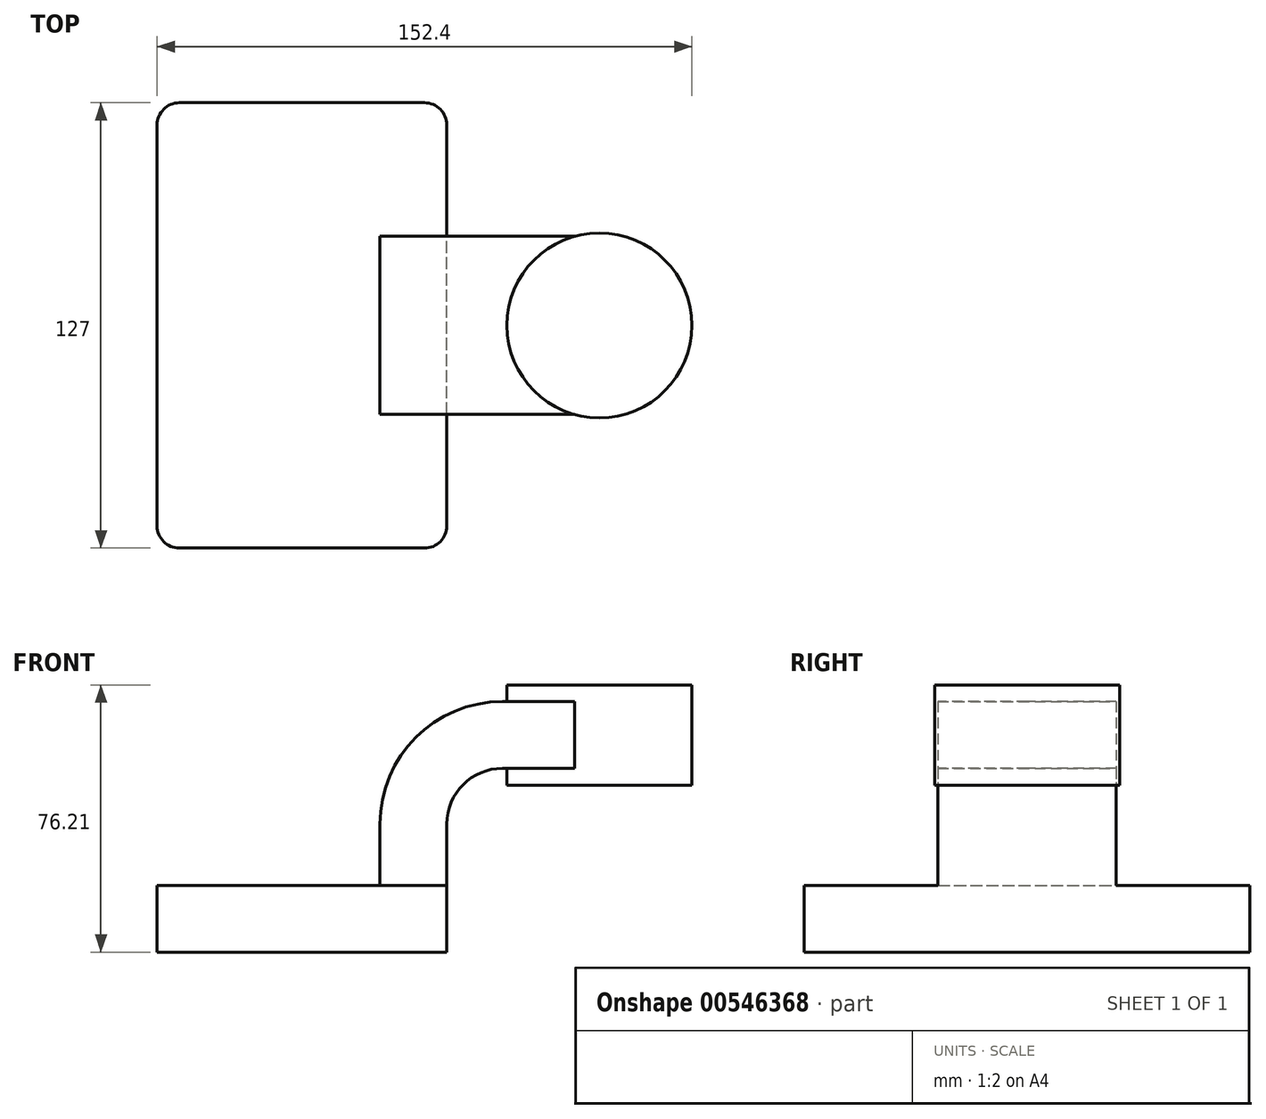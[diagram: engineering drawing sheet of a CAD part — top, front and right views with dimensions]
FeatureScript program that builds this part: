
annotation { "Feature Type Name" : "Feature", "Feature Type Description" : "" }
export const myFeature = defineFeature(function(context is Context, id is Id, definition is map)
    precondition{}
    {
        {
            var Q0;
            Q0=qCreatedBy(makeId("Front.planeOp"),FACE);
            var sketch = newSketch(context, id + "F0", { "sketchPlane" : qUnion([Q0])});
            skLineSegment(sketch, "E0.bottom", {"start": v(-41.28, -9.53) * mm, "end": v(41.28, -9.53) * mm});
            skLineSegment(sketch, "E0.top", {"start": v(-41.28, 9.53) * mm, "end": v(41.27, 9.53) * mm});
            skLineSegment(sketch, "E0.left", {"start": v(-41.27, -9.53) * mm, "end": v(-41.28, 9.53) * mm});
            skLineSegment(sketch, "E0.right", {"start": v(41.28, -9.53) * mm, "end": v(41.27, 9.53) * mm});
            skPoint(sketch, "E0.middle", {"position": v(0, 0) * mm});
            skLineSegment(sketch, "E1.bottom", {"start": v(60.32, 38.1) * mm, "end": v(111.12, 38.1) * mm});
            skLineSegment(sketch, "E1.top", {"start": v(60.32, 66.67) * mm, "end": v(111.12, 66.67) * mm});
            skLineSegment(sketch, "E1.left", {"start": v(60.32, 38.1) * mm, "end": v(60.32, 66.67) * mm});
            skLineSegment(sketch, "E1.right", {"start": v(111.12, 38.1) * mm, "end": v(111.12, 66.67) * mm});
            skPoint(sketch, "E1.middle", {"position": v(85.72, 52.39) * mm});
            skLineSegment(sketch, "E2", {"start": v(41.27, 9.52) * mm, "end": v(41.27, 27) * mm});
            skArc(sketch, "E3", {"start": v(41.27, 27) * mm, "mid": v(45.92, 38.23) * mm, "end": v(57.15, 42.88) * mm});
            skLineSegment(sketch, "E4", {"start": v(57.15, 42.88) * mm, "end": v(84.76, 42.88) * mm});
            skLineSegment(sketch, "E5.0", {"start": v(57.15, 61.93) * mm, "end": v(84.76, 61.93) * mm});
            skArc(sketch, "E5.1", {"start": v(22.22, 27) * mm, "mid": v(32.45, 51.7) * mm, "end": v(57.15, 61.93) * mm});
            skLineSegment(sketch, "E5.2", {"start": v(22.22, 9.52) * mm, "end": v(22.22, 27) * mm});
            skLineSegment(sketch, "E6", {"start": v(84.76, 42.88) * mm, "end": v(84.76, 61.93) * mm});
            skFitSpline(sketch, "E7", {"points": [v(-41.28, 9.53) * mm, v(57.15, 61.93) * mm], "startDerivative": vector(0.3, 45.38) * mm, "endDerivative": vector(126.17, -10.41) * mm});
            skLineSegment(sketch, "E8", {"start": v(84.76, 61.93) * mm, "end": v(84.76, 38.1) * mm});
            skLineSegment(sketch, "E9", {"start": v(84.76, 38.1) * mm, "end": v(84.76, 66.67) * mm});
            skSolve(sketch);
        }
        {
            var Q0;
            Q0=makeQuery(id+"F0.imprint","IMPRINT",FACE,{"disambiguationData":[TD([[makeQuery(id+"F0.imprint","IMPRINT",EDGE,{"derivedFrom":sQuery(id+"F0.wireOp",EDGE,"E0.bottom")}),1.0]])]});
            extrude(context, id + "F1", {"entities" : qUnion([Q0]), "endBound" : BoundingType.SYMMETRIC, "depth" : 127 * mm, "offsetDistance" : 25.4 * mm});
        }
        {
            var Q0;
            {var subQ0=sQuery(id+"F0.wireOp",EDGE,"E2");Q0=makeQuery(id+"F0.imprint","IMPRINT",FACE,{"disambiguationData":[TD([[makeQuery(id+"F0.imprint","IMPRINT",EDGE,{"derivedFrom":subQ0}),1.0]])]});}
            var Q1;
            {var subQ5=sQuery(id+"F0.wireOp",EDGE,"E6");Q1=makeQuery(id+"F0.imprint","IMPRINT",FACE,{"disambiguationData":[TD([[makeQuery(id+"F0.imprint","IMPRINT",EDGE,{"derivedFrom":subQ5}),1.0]])]});}
            extrude(context, id + "F2", {"entities" : qUnion([Q0, Q1]), "operationType" : NewBodyOperationType.ADD, "endBound" : BoundingType.SYMMETRIC, "depth" : 50.8 * mm, "offsetDistance" : 25.4 * mm});
        }
        {
            var Q0;
            Q0=makeQuery(id+"F0.imprint","IMPRINT",FACE,{"disambiguationData":[TD([[makeQuery(id+"F0.imprint","IMPRINT",EDGE,{"derivedFrom":sQuery(id+"F0.wireOp",EDGE,"E5.1")}),1.0]])]});
            extrude(context, id + "F3", {"entities" : qUnion([Q0]), "operationType" : NewBodyOperationType.ADD, "endBound" : BoundingType.SYMMETRIC, "depth" : 25.4 * mm, "offsetDistance" : 25.4 * mm});
        }
        {
            var Q0;
            {var subQ0=sQuery(id+"F0.wireOp",EDGE,"E4");var subQ1=sQuery(id+"F0.wireOp",EDGE,"E1.left");var subQ2=makeQuery(id+"F0.imprint","INTERSECT",VERTEX,{"derivedFrom":[subQ1,subQ0]});Q0=makeQuery(id+"F0.imprint","IMPRINT",FACE,{"disambiguationData":[TD([[makeQuery(id+"F0.imprint","IMPRINT",EDGE,{"disambiguationData":[TD([[subQ2,-1.0]])],"derivedFrom":subQ1}),-1.0]])]});}
            extrude(context, id + "F4", {"entities" : qUnion([Q0]), "operationType" : NewBodyOperationType.ADD, "endBound" : BoundingType.SYMMETRIC, "depth" : 50.8 * mm, "offsetDistance" : 25.4 * mm});
        }
        {
            var Q0;
            {var subQ4=sQuery(id+"F0.wireOp",EDGE,"E1.right");Q0=makeQuery(id+"F0.imprint","IMPRINT",FACE,{"disambiguationData":[TD([[makeQuery(id+"F0.imprint","IMPRINT",EDGE,{"derivedFrom":subQ4}),1.0]])]});}
            var Q1;
            Q1=sQuery(id+"F0.wireOp",EDGE,"E9");
            revolve(context, id + "F5", {"operationType" : NewBodyOperationType.ADD, "entities" : qUnion([Q0]), "axis" : qUnion([Q1]), "revolveType" : RevolveType.FULL});
        }
        {
            var Q0;
            Q0=makeQuery(id+"F1.opExtrude","CAP_EDGE",EDGE,{"disambiguationData":[OSD([sQuery(id+"F0.wireOp",EDGE,"E0.left")])],"isStart":false});
            var Q1;
            Q1=makeQuery(id+"F1.opExtrude","CAP_EDGE",EDGE,{"disambiguationData":[OSD([sQuery(id+"F0.wireOp",EDGE,"E0.right")])],"isStart":false});
            var Q2;
            Q2=makeQuery(id+"F1.opExtrude","CAP_EDGE",EDGE,{"disambiguationData":[OSD([sQuery(id+"F0.wireOp",EDGE,"E0.right")])],"isStart":true});
            var Q3;
            Q3=makeQuery(id+"F1.opExtrude","CAP_EDGE",EDGE,{"disambiguationData":[OSD([sQuery(id+"F0.wireOp",EDGE,"E0.left")])],"isStart":true});
            fillet(context, id + "F6", {"entities" : qUnion([Q0, Q1, Q2, Q3]), "radius" : 6.35 * mm, "tangentPropagation" : true, "allowEdgeOverflow" : false});
        }
    });
